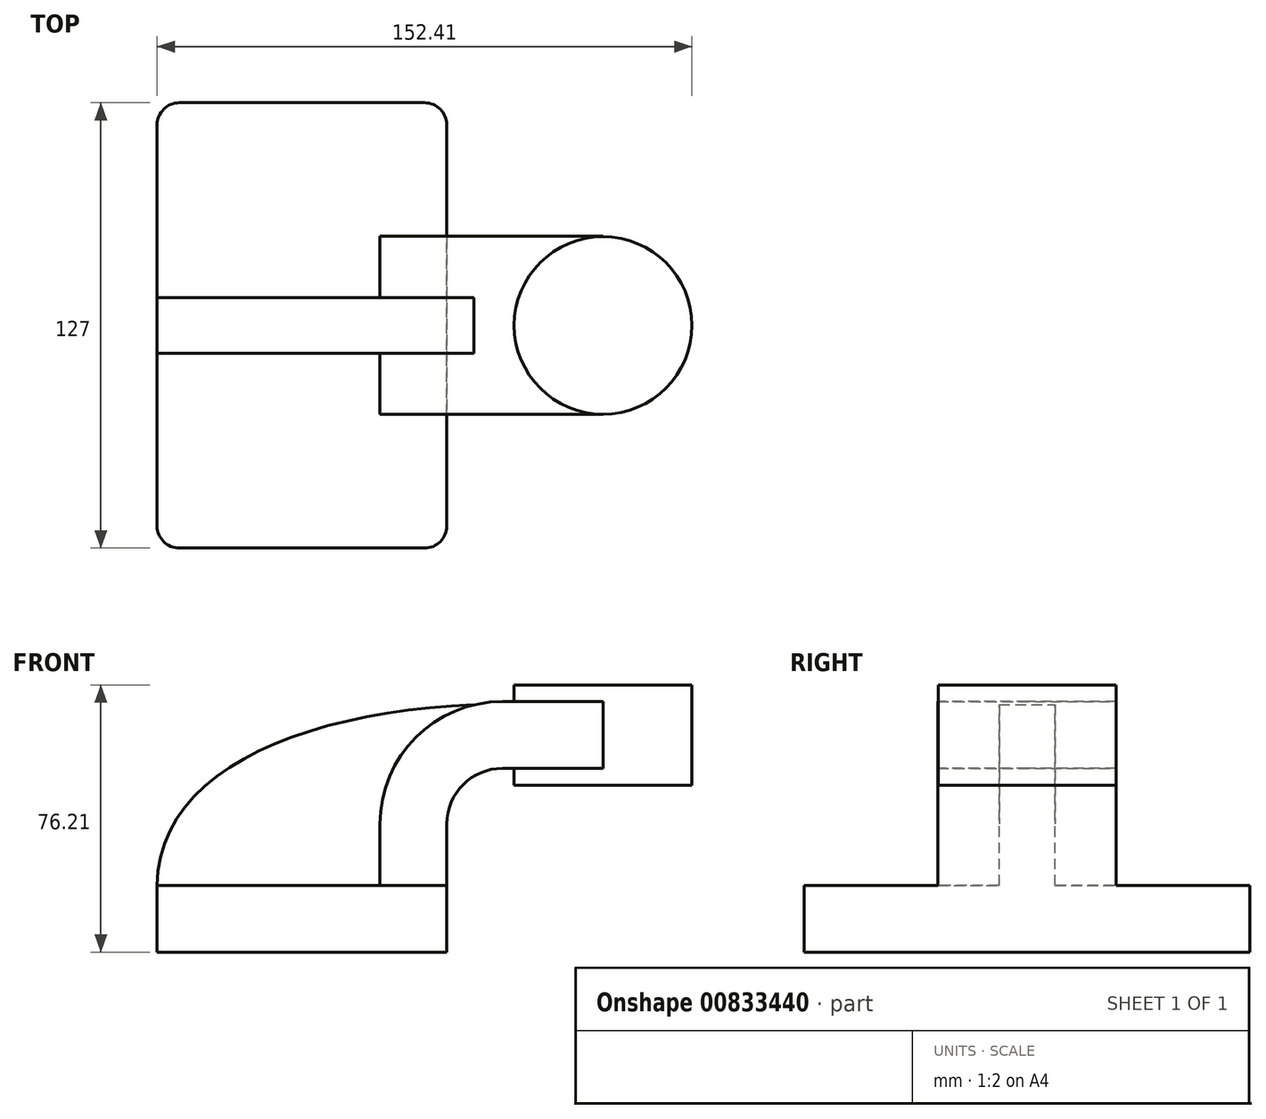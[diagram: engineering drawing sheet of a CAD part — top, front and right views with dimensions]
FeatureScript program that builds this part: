
annotation { "Feature Type Name" : "Feature", "Feature Type Description" : "" }
export const myFeature = defineFeature(function(context is Context, id is Id, definition is map)
    precondition{}
    {
        {
            var Q0;
            Q0=qCreatedBy(makeId("Front.planeOp"),FACE);
            var sketch = newSketch(context, id + "F0", { "sketchPlane" : qUnion([Q0])});
            skLineSegment(sketch, "E0.bottom", {"start": v(41.27, 9.52) * mm, "end": v(-41.27, 9.53) * mm});
            skLineSegment(sketch, "E0.top", {"start": v(41.27, -9.53) * mm, "end": v(-41.27, -9.52) * mm});
            skLineSegment(sketch, "E0.left", {"start": v(41.27, 9.52) * mm, "end": v(41.27, -9.52) * mm});
            skLineSegment(sketch, "E0.right", {"start": v(-41.27, 9.53) * mm, "end": v(-41.27, -9.52) * mm});
            skPoint(sketch, "E0.middle", {"position": v(0, 0) * mm});
            skLineSegment(sketch, "E1.bottom", {"start": v(111.13, 38.1) * mm, "end": v(60.33, 38.1) * mm});
            skLineSegment(sketch, "E1.top", {"start": v(111.13, 66.67) * mm, "end": v(60.33, 66.67) * mm});
            skLineSegment(sketch, "E1.left", {"start": v(111.13, 38.1) * mm, "end": v(111.13, 66.68) * mm});
            skLineSegment(sketch, "E1.right", {"start": v(60.33, 38.1) * mm, "end": v(60.33, 66.68) * mm});
            skPoint(sketch, "E1.middle", {"position": v(85.72, 52.39) * mm});
            skLineSegment(sketch, "E2", {"start": v(41.27, 9.52) * mm, "end": v(41.27, 27) * mm});
            skArc(sketch, "E3", {"start": v(41.28, 27) * mm, "mid": v(45.92, 38.23) * mm, "end": v(57.15, 42.88) * mm});
            skLineSegment(sketch, "E4", {"start": v(57.15, 42.88) * mm, "end": v(85.8, 42.88) * mm});
            skArc(sketch, "E5.1", {"start": v(22.23, 27) * mm, "mid": v(32.45, 51.7) * mm, "end": v(57.15, 61.93) * mm});
            skLineSegment(sketch, "E5.2", {"start": v(22.23, 9.52) * mm, "end": v(22.23, 27) * mm});
            skLineSegment(sketch, "E6", {"start": v(85.8, 38.1) * mm, "end": v(85.8, 66.67) * mm});
            skFitSpline(sketch, "E7", {"points": [v(-41.27, 9.53) * mm, v(49.04, 60.97) * mm], "startDerivative": vector(0.3, 96.9) * mm, "endDerivative": vector(147.13, 5.44) * mm});
            skLineSegment(sketch, "E8", {"start": v(57.15, 61.93) * mm, "end": v(85.8, 61.93) * mm});
            skSolve(sketch);
        }
        {
            var Q0;
            Q0=makeQuery(id+"F0.imprint","IMPRINT",FACE,{"disambiguationData":[TD([[makeQuery(id+"F0.imprint","IMPRINT",EDGE,{"derivedFrom":sQuery(id+"F0.wireOp",EDGE,"E0.top")}),-1.0]])]});
            extrude(context, id + "F1", {"entities" : qUnion([Q0]), "endBound" : BoundingType.SYMMETRIC, "oppositeDirection" : true, "depth" : 127 * mm, "offsetDistance" : 25.4 * mm});
        }
        {
            var Q0;
            {var subQ1=sQuery(id+"F0.wireOp",EDGE,"E2");Q0=makeQuery(id+"F0.imprint","IMPRINT",FACE,{"disambiguationData":[TD([[makeQuery(id+"F0.imprint","IMPRINT",EDGE,{"derivedFrom":subQ1}),1.0]])]});}
            var Q1;
            {var subQ0=sQuery(id+"F0.wireOp",EDGE,"E4");var subQ1=sQuery(id+"F0.wireOp",EDGE,"E1.right");var subQ2=makeQuery(id+"F0.imprint","INTERSECT",VERTEX,{"derivedFrom":[subQ1,subQ0]});Q1=makeQuery(id+"F0.imprint","IMPRINT",FACE,{"disambiguationData":[TD([[makeQuery(id+"F0.imprint","IMPRINT",EDGE,{"disambiguationData":[TD([[subQ2,-1.0]])],"derivedFrom":subQ1}),-1.0]])]});}
            extrude(context, id + "F2", {"entities" : qUnion([Q0, Q1]), "operationType" : NewBodyOperationType.ADD, "endBound" : BoundingType.SYMMETRIC, "depth" : 50.8 * mm, "offsetDistance" : 25.4 * mm});
        }
        {
            var Q0;
            {var subQ2=sQuery(id+"F0.wireOp",EDGE,"E5.2");Q0=makeQuery(id+"F0.imprint","IMPRINT",FACE,{"disambiguationData":[TD([[makeQuery(id+"F0.imprint","IMPRINT",EDGE,{"derivedFrom":subQ2}),1.0]])]});}
            extrude(context, id + "F3", {"entities" : qUnion([Q0]), "operationType" : NewBodyOperationType.ADD, "endBound" : BoundingType.SYMMETRIC, "depth" : 15.88 * mm, "offsetDistance" : 25.4 * mm});
        }
        {
            var Q0;
            {var subQ0=sQuery(id+"F0.wireOp",EDGE,"E1.left");Q0=makeQuery(id+"F0.imprint","IMPRINT",FACE,{"disambiguationData":[TD([[makeQuery(id+"F0.imprint","IMPRINT",EDGE,{"derivedFrom":subQ0}),1.0]])]});}
            var Q1;
            Q1=sQuery(id+"F0.wireOp",EDGE,"E6");
            revolve(context, id + "F4", {"operationType" : NewBodyOperationType.ADD, "surfaceOperationType" : NewSurfaceOperationType.NEW, "entities" : qUnion([Q0]), "axis" : qUnion([Q1]), "revolveType" : RevolveType.FULL});
        }
        {
            var Q0;
            Q0=makeQuery(id+"F1.opExtrude","CAP_EDGE",EDGE,{"disambiguationData":[OSD([sQuery(id+"F0.wireOp",EDGE,"E0.left")])],"isStart":true});
            var Q1;
            Q1=makeQuery(id+"F1.opExtrude","CAP_EDGE",EDGE,{"disambiguationData":[OSD([sQuery(id+"F0.wireOp",EDGE,"E0.left")])],"isStart":false});
            var Q2;
            Q2=makeQuery(id+"F1.opExtrude","CAP_EDGE",EDGE,{"disambiguationData":[OSD([sQuery(id+"F0.wireOp",EDGE,"E0.right")])],"isStart":false});
            var Q3;
            Q3=makeQuery(id+"F1.opExtrude","CAP_EDGE",EDGE,{"disambiguationData":[OSD([sQuery(id+"F0.wireOp",EDGE,"E0.right")])],"isStart":true});
            fillet(context, id + "F5", {"entities" : qUnion([Q0, Q1, Q2, Q3]), "radius" : 6.35 * mm, "tangentPropagation" : true, "allowEdgeOverflow" : false});
        }
    });
